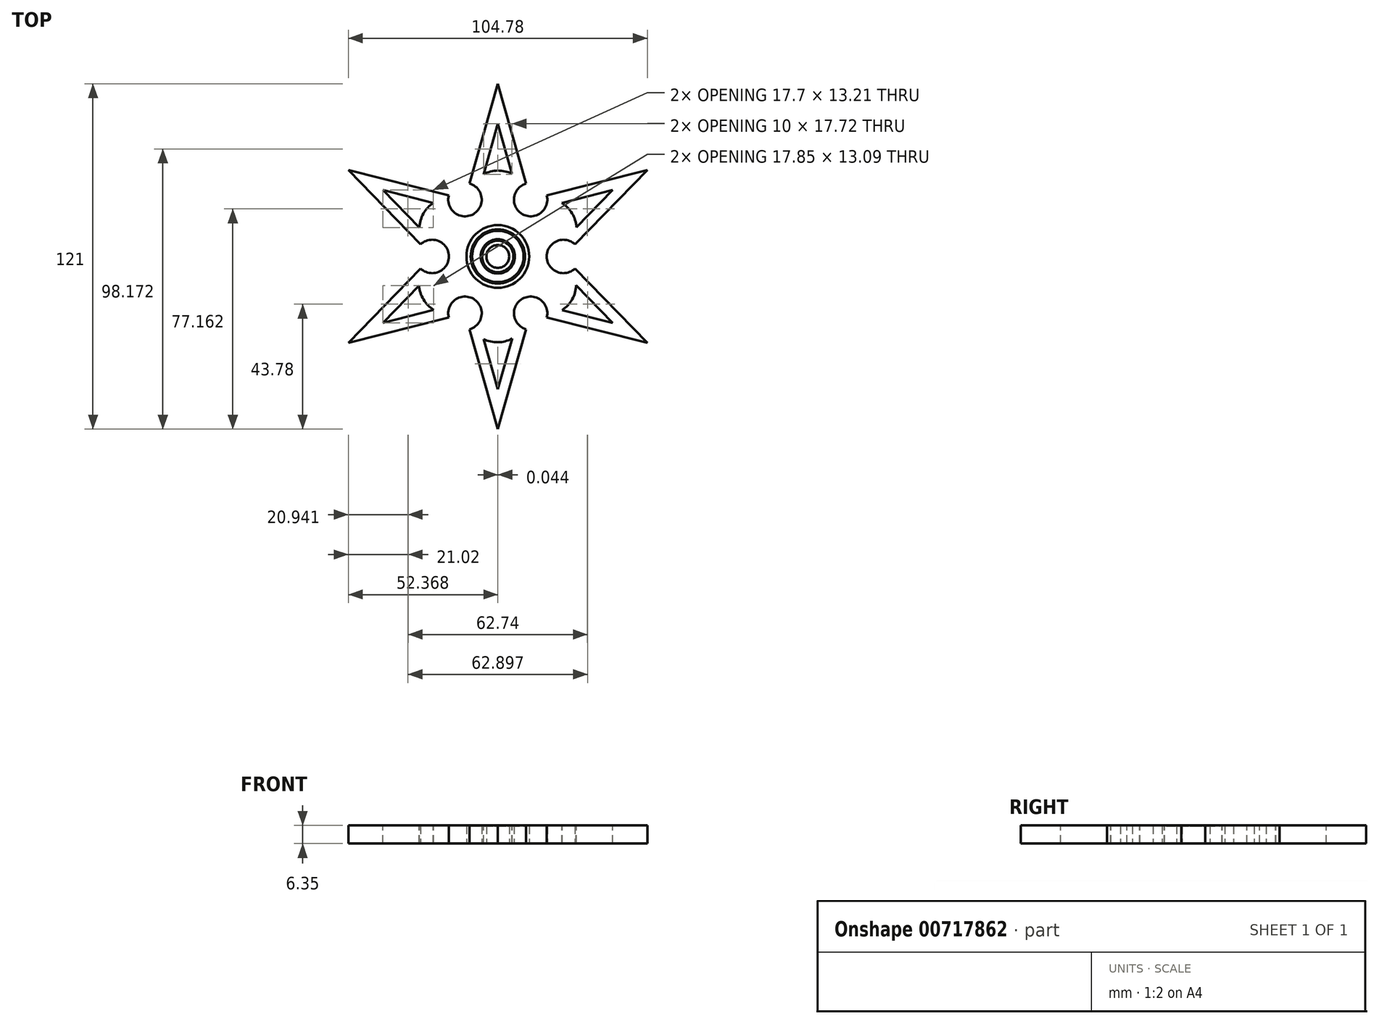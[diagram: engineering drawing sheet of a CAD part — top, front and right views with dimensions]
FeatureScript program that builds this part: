
annotation { "Feature Type Name" : "Feature", "Feature Type Description" : "" }
export const myFeature = defineFeature(function(context is Context, id is Id, definition is map)
    precondition{}
    {
        {
            assignVariable(context, id + "F0", {"name" : "th", "anyValue" : 6.35 * mm});
        }
        {
            var Q0;
            Q0=qCreatedBy(makeId("Top.planeOp"),FACE);
            var sketch = newSketch(context, id + "F1", { "sketchPlane" : qUnion([Q0])});
            skCircle(sketch, "E0", {"center": v(0, 0) * mm, "radius": 4 * mm});
            skCircle(sketch, "E1", {"center": v(0, 0) * mm, "radius": 11 * mm});
            skSolve(sketch);
        }
        {
            var Q0;
            Q0=makeQuery(id+"F1.imprint","IMPRINT",FACE,{"disambiguationData":[TD([[makeQuery(id+"F1.imprint","IMPRINT",EDGE,{"derivedFrom":sQuery(id+"F1.wireOp",EDGE,"E0")}),-1.0]])]});
            extrude(context, id + "F2", {"entities" : qUnion([Q0]), "depth" : getVariable(context, 'th'), "offsetDistance" : 25.4 * mm});
        }
        {
            var Q0;
            Q0=qCreatedBy(makeId("Right.planeOp"),FACE);
            var sketch = newSketch(context, id + "F3", { "sketchPlane" : qUnion([Q0])});
            skLineSegment(sketch, "E2", {"start": v(0, 0) * mm, "end": v(0, 6.35) * mm});
            skLineSegment(sketch, "E3", {"start": v(0, 6.35) * mm, "end": v(4, 6.35) * mm});
            skLineSegment(sketch, "E4", {"start": v(4, 6.35) * mm, "end": v(5.75, 6.35) * mm});
            skLineSegment(sketch, "E5", {"start": v(5.75, 6.35) * mm, "end": v(9.25, 6.35) * mm});
            skLineSegment(sketch, "E6", {"start": v(9.25, 6.35) * mm, "end": v(11, 6.35) * mm});
            skCircle(sketch, "E7", {"center": v(5.75, 6.35) * mm, "radius": 0.25 * mm});
            skCircle(sketch, "E8", {"center": v(9.25, 6.35) * mm, "radius": 0.25 * mm});
            skSolve(sketch);
        }
        {
            var Q0;
            Q0 = qSketchRegion(id + "F3", true);
            var Q1;
            Q1=sQuery(id+"F3.wireOp",EDGE,"E2");
            revolve(context, id + "F4", {"operationType" : NewBodyOperationType.REMOVE, "surfaceOperationType" : NewSurfaceOperationType.NEW, "entities" : qUnion([Q0]), "axis" : qUnion([Q1]), "revolveType" : RevolveType.FULL, "oppositeDirection" : true});
        }
        {
            var Q0;
            Q0=qCreatedBy(makeId("Top.planeOp"),FACE);
            var sketch = newSketch(context, id + "F5", { "sketchPlane" : qUnion([Q0])});
            skCircle(sketch, "E9", {"center": v(0, 0) * mm, "radius": 16.5 * mm});
            skLineSegment(sketch, "E10", {"start": v(0, 16.5) * mm, "end": v(0, 60.5) * mm});
            skLineSegment(sketch, "E11", {"start": v(0, 60.5) * mm, "end": v(9.9, 25.56) * mm});
            skLineSegment(sketch, "E12", {"start": v(0, 60.5) * mm, "end": v(-9.9, 25.56) * mm});
            skLineSegment(sketch, "E13.1.0", {"start": v(-52.4, 30.25) * mm, "end": v(-17.18, 21.36) * mm});
            skLineSegment(sketch, "E13.1.1", {"start": v(-52.4, 30.25) * mm, "end": v(-27.08, 4.2) * mm});
            skLineSegment(sketch, "E13.2.0", {"start": v(-52.4, -30.25) * mm, "end": v(-27.08, -4.2) * mm});
            skLineSegment(sketch, "E13.2.1", {"start": v(-52.4, -30.25) * mm, "end": v(-17.18, -21.36) * mm});
            skLineSegment(sketch, "E14.2.3.0", {"start": v(0, -60.5) * mm, "end": v(-9.9, -25.56) * mm});
            skLineSegment(sketch, "E14.3.3.0", {"start": v(0, -60.5) * mm, "end": v(9.9, -25.56) * mm});
            skLineSegment(sketch, "E14.2.4.0", {"start": v(52.4, -30.25) * mm, "end": v(17.18, -21.36) * mm});
            skLineSegment(sketch, "E14.3.4.0", {"start": v(52.4, -30.25) * mm, "end": v(27.08, -4.2) * mm});
            skLineSegment(sketch, "E14.2.5.0", {"start": v(52.4, 30.25) * mm, "end": v(27.08, 4.2) * mm});
            skLineSegment(sketch, "E14.3.5.0", {"start": v(52.4, 30.25) * mm, "end": v(17.18, 21.36) * mm});
            skArc(sketch, "E15", {"start": v(17.18, -21.36) * mm, "mid": v(8.58, -14.85) * mm, "end": v(9.9, -25.56) * mm});
            skArc(sketch, "E16.1.0", {"start": v(27.08, 4.2) * mm, "mid": v(17.15, 0) * mm, "end": v(27.08, -4.2) * mm});
            skArc(sketch, "E16.2.0", {"start": v(9.9, 25.56) * mm, "mid": v(8.58, 14.85) * mm, "end": v(17.18, 21.36) * mm});
            skArc(sketch, "E17.1.3.0", {"start": v(-17.18, 21.36) * mm, "mid": v(-8.58, 14.85) * mm, "end": v(-9.9, 25.56) * mm});
            skArc(sketch, "E17.1.4.0", {"start": v(-27.08, -4.2) * mm, "mid": v(-17.15, 0) * mm, "end": v(-27.08, 4.2) * mm});
            skArc(sketch, "E17.1.5.0", {"start": v(-9.9, -25.56) * mm, "mid": v(-8.58, -14.85) * mm, "end": v(-17.18, -21.36) * mm});
            skLineSegment(sketch, "E18.trimOffspring", {"start": v(-5.83, -18.49) * mm, "end": v(8.58, -14.85) * mm});
            skLineSegment(sketch, "E19.trimOffspring", {"start": v(-13.1, -14.29) * mm, "end": v(-17.15, 0) * mm});
            skLineSegment(sketch, "E20.trimOffspring", {"start": v(-18.93, 4.2) * mm, "end": v(-8.58, 14.85) * mm});
            skLineSegment(sketch, "E21.trimOffspring", {"start": v(-18.93, -4.2) * mm, "end": v(-8.58, -14.85) * mm});
            skLineSegment(sketch, "E22.trimOffspring", {"start": v(-13.1, 14.29) * mm, "end": v(-17.15, 0) * mm});
            skLineSegment(sketch, "E23.trimOffspring", {"start": v(-5.83, 18.49) * mm, "end": v(8.58, 14.85) * mm});
            skLineSegment(sketch, "E24.trimOffspring", {"start": v(13.1, -14.29) * mm, "end": v(17.15, 0) * mm});
            skLineSegment(sketch, "E25.trimOffspring", {"start": v(5.83, -18.49) * mm, "end": v(-8.58, -14.85) * mm});
            skLineSegment(sketch, "E26.trimOffspring", {"start": v(5.83, 18.49) * mm, "end": v(-8.58, 14.85) * mm});
            skLineSegment(sketch, "E27.trimOffspring", {"start": v(13.1, 14.29) * mm, "end": v(17.15, 0) * mm});
            skLineSegment(sketch, "E28.trimOffspring", {"start": v(18.93, 4.2) * mm, "end": v(8.58, 14.85) * mm});
            skLineSegment(sketch, "E29.trimOffspring", {"start": v(18.93, -4.2) * mm, "end": v(8.58, -14.85) * mm});
            skCircle(sketch, "E30", {"center": v(0, 0) * mm, "radius": 11 * mm});
            skSolve(sketch);
        }
        {
            var Q0;
            {var subQ0=sQuery(id+"F5.wireOp",EDGE,"E11");Q0=makeQuery(id+"F5.imprint","IMPRINT",FACE,{"disambiguationData":[TD([[makeQuery(id+"F5.imprint","IMPRINT",EDGE,{"derivedFrom":subQ0}),-1.0]])]});}
            var Q1;
            {var subQ0=sQuery(id+"F5.wireOp",EDGE,"E12");Q1=makeQuery(id+"F5.imprint","IMPRINT",FACE,{"disambiguationData":[TD([[makeQuery(id+"F5.imprint","IMPRINT",EDGE,{"derivedFrom":subQ0}),1.0]])]});}
            var Q2;
            {var subQ7=sQuery(id+"F5.wireOp",EDGE,"E13.1.0");Q2=makeQuery(id+"F5.imprint","IMPRINT",FACE,{"disambiguationData":[TD([[makeQuery(id+"F5.imprint","IMPRINT",EDGE,{"derivedFrom":subQ7}),-1.0]])]});}
            var Q3;
            {var subQ4=sQuery(id+"F5.wireOp",EDGE,"E13.2.0");Q3=makeQuery(id+"F5.imprint","IMPRINT",FACE,{"disambiguationData":[TD([[makeQuery(id+"F5.imprint","IMPRINT",EDGE,{"derivedFrom":subQ4}),-1.0]])]});}
            var Q4;
            {var subQ1=sQuery(id+"F5.wireOp",EDGE,"E14.2.3.0");Q4=makeQuery(id+"F5.imprint","IMPRINT",FACE,{"disambiguationData":[TD([[makeQuery(id+"F5.imprint","IMPRINT",EDGE,{"derivedFrom":subQ1}),-1.0]])]});}
            var Q5;
            {var subQ5=sQuery(id+"F5.wireOp",EDGE,"E14.2.4.0");Q5=makeQuery(id+"F5.imprint","IMPRINT",FACE,{"disambiguationData":[TD([[makeQuery(id+"F5.imprint","IMPRINT",EDGE,{"derivedFrom":subQ5}),-1.0]])]});}
            var Q6;
            {var subQ1=sQuery(id+"F5.wireOp",EDGE,"E14.2.5.0");Q6=makeQuery(id+"F5.imprint","IMPRINT",FACE,{"disambiguationData":[TD([[makeQuery(id+"F5.imprint","IMPRINT",EDGE,{"derivedFrom":subQ1}),-1.0]])]});}
            var Q7;
            {var subQ0=sQuery(id+"F5.wireOp",EDGE,"E24.trimOffspring");var subQ1=sQuery(id+"F5.wireOp",EDGE,"E9");var subQ2=makeQuery(id+"F5.imprint","INTERSECT",VERTEX,{"derivedFrom":[subQ1,subQ0]});Q7=makeQuery(id+"F5.imprint","IMPRINT",FACE,{"disambiguationData":[TD([[makeQuery(id+"F5.imprint","IMPRINT",EDGE,{"disambiguationData":[TD([[subQ2,-1.0]])],"derivedFrom":subQ1}),-1.0]])]});}
            var Q8;
            {var subQ0=sQuery(id+"F5.wireOp",EDGE,"E28.trimOffspring");var subQ1=sQuery(id+"F5.wireOp",EDGE,"E9");var subQ2=makeQuery(id+"F5.imprint","INTERSECT",VERTEX,{"derivedFrom":[subQ1,subQ0]});Q8=makeQuery(id+"F5.imprint","IMPRINT",FACE,{"disambiguationData":[TD([[makeQuery(id+"F5.imprint","IMPRINT",EDGE,{"disambiguationData":[TD([[subQ2,-1.0]])],"derivedFrom":subQ1}),-1.0]])]});}
            var Q9;
            {var subQ0=sQuery(id+"F5.wireOp",EDGE,"E26.trimOffspring");var subQ1=sQuery(id+"F5.wireOp",EDGE,"E9");var subQ2=makeQuery(id+"F5.imprint","INTERSECT",VERTEX,{"derivedFrom":[subQ1,subQ0]});Q9=makeQuery(id+"F5.imprint","IMPRINT",FACE,{"disambiguationData":[TD([[makeQuery(id+"F5.imprint","IMPRINT",EDGE,{"disambiguationData":[TD([[subQ2,-1.0]])],"derivedFrom":subQ1}),-1.0]])]});}
            var Q10;
            {var subQ0=sQuery(id+"F5.wireOp",EDGE,"E22.trimOffspring");var subQ1=sQuery(id+"F5.wireOp",EDGE,"E9");var subQ2=makeQuery(id+"F5.imprint","INTERSECT",VERTEX,{"derivedFrom":[subQ1,subQ0]});Q10=makeQuery(id+"F5.imprint","IMPRINT",FACE,{"disambiguationData":[TD([[makeQuery(id+"F5.imprint","IMPRINT",EDGE,{"disambiguationData":[TD([[subQ2,-1.0]])],"derivedFrom":subQ1}),-1.0]])]});}
            var Q11;
            {var subQ0=sQuery(id+"F5.wireOp",EDGE,"E21.trimOffspring");var subQ1=sQuery(id+"F5.wireOp",EDGE,"E9");var subQ2=makeQuery(id+"F5.imprint","INTERSECT",VERTEX,{"derivedFrom":[subQ1,subQ0]});Q11=makeQuery(id+"F5.imprint","IMPRINT",FACE,{"disambiguationData":[TD([[makeQuery(id+"F5.imprint","IMPRINT",EDGE,{"disambiguationData":[TD([[subQ2,-1.0]])],"derivedFrom":subQ1}),-1.0]])]});}
            var Q12;
            {var subQ0=sQuery(id+"F5.wireOp",EDGE,"E29.trimOffspring");var subQ1=sQuery(id+"F5.wireOp",EDGE,"E9");var subQ2=makeQuery(id+"F5.imprint","INTERSECT",VERTEX,{"derivedFrom":[subQ1,subQ0]});Q12=makeQuery(id+"F5.imprint","IMPRINT",FACE,{"disambiguationData":[TD([[makeQuery(id+"F5.imprint","IMPRINT",EDGE,{"disambiguationData":[TD([[subQ2,1.0]])],"derivedFrom":subQ1}),-1.0]])]});}
            var Q13;
            {var subQ1=sQuery(id+"F5.wireOp",EDGE,"E15");var subQ3=sQuery(id+"F5.wireOp",EDGE,"E24.trimOffspring");var subQ4=makeQuery(id+"F5.imprint","INTERSECT",VERTEX,{"derivedFrom":[subQ1,subQ3]});Q13=makeQuery(id+"F5.imprint","IMPRINT",FACE,{"disambiguationData":[TD([[makeQuery(id+"F5.imprint","IMPRINT",EDGE,{"disambiguationData":[TD([[subQ4,-1.0]])],"derivedFrom":subQ3}),1.0]])]});}
            var Q14;
            {var subQ0=sQuery(id+"F5.wireOp",EDGE,"E18.trimOffspring");var subQ5=makeQuery(id+"F5.imprint","INTERSECT",VERTEX,{"derivedFrom":[sQuery(id+"F5.wireOp",EDGE,"E9"),subQ0]});Q14=makeQuery(id+"F5.imprint","IMPRINT",FACE,{"disambiguationData":[TD([[makeQuery(id+"F5.imprint","IMPRINT",EDGE,{"disambiguationData":[TD([[subQ5,1.0]])],"derivedFrom":subQ0}),-1.0]])]});}
            var Q15;
            {var subQ0=sQuery(id+"F5.wireOp",EDGE,"E27.trimOffspring");var subQ5=makeQuery(id+"F5.imprint","INTERSECT",VERTEX,{"derivedFrom":[sQuery(id+"F5.wireOp",EDGE,"E9"),subQ0]});Q15=makeQuery(id+"F5.imprint","IMPRINT",FACE,{"disambiguationData":[TD([[makeQuery(id+"F5.imprint","IMPRINT",EDGE,{"disambiguationData":[TD([[subQ5,1.0]])],"derivedFrom":subQ0}),1.0]])]});}
            var Q16;
            {var subQ0=sQuery(id+"F5.wireOp",EDGE,"E24.trimOffspring");var subQ5=makeQuery(id+"F5.imprint","INTERSECT",VERTEX,{"derivedFrom":[sQuery(id+"F5.wireOp",EDGE,"E9"),subQ0]});Q16=makeQuery(id+"F5.imprint","IMPRINT",FACE,{"disambiguationData":[TD([[makeQuery(id+"F5.imprint","IMPRINT",EDGE,{"disambiguationData":[TD([[subQ5,1.0]])],"derivedFrom":subQ0}),-1.0]])]});}
            var Q17;
            {var subQ1=sQuery(id+"F5.wireOp",EDGE,"E16.2.0");var subQ3=sQuery(id+"F5.wireOp",EDGE,"E27.trimOffspring");var subQ4=makeQuery(id+"F5.imprint","INTERSECT",VERTEX,{"derivedFrom":[subQ1,subQ3]});Q17=makeQuery(id+"F5.imprint","IMPRINT",FACE,{"disambiguationData":[TD([[makeQuery(id+"F5.imprint","IMPRINT",EDGE,{"disambiguationData":[TD([[subQ4,-1.0]])],"derivedFrom":subQ3}),-1.0]])]});}
            var Q18;
            {var subQ0=sQuery(id+"F5.wireOp",EDGE,"E20.trimOffspring");var subQ5=makeQuery(id+"F5.imprint","INTERSECT",VERTEX,{"derivedFrom":[sQuery(id+"F5.wireOp",EDGE,"E9"),subQ0]});Q18=makeQuery(id+"F5.imprint","IMPRINT",FACE,{"disambiguationData":[TD([[makeQuery(id+"F5.imprint","IMPRINT",EDGE,{"disambiguationData":[TD([[subQ5,1.0]])],"derivedFrom":subQ0}),1.0]])]});}
            var Q19;
            {var subQ1=sQuery(id+"F5.wireOp",EDGE,"E17.1.3.0");var subQ3=sQuery(id+"F5.wireOp",EDGE,"E23.trimOffspring");var subQ4=makeQuery(id+"F5.imprint","INTERSECT",VERTEX,{"derivedFrom":[subQ1,subQ3]});Q19=makeQuery(id+"F5.imprint","IMPRINT",FACE,{"disambiguationData":[TD([[makeQuery(id+"F5.imprint","IMPRINT",EDGE,{"disambiguationData":[TD([[subQ4,1.0]])],"derivedFrom":subQ1}),-1.0]])]});}
            var Q20;
            {var subQ0=sQuery(id+"F5.wireOp",EDGE,"E19.trimOffspring");var subQ5=makeQuery(id+"F5.imprint","INTERSECT",VERTEX,{"derivedFrom":[sQuery(id+"F5.wireOp",EDGE,"E9"),subQ0]});Q20=makeQuery(id+"F5.imprint","IMPRINT",FACE,{"disambiguationData":[TD([[makeQuery(id+"F5.imprint","IMPRINT",EDGE,{"disambiguationData":[TD([[subQ5,1.0]])],"derivedFrom":subQ0}),1.0]])]});}
            var Q21;
            {var subQ1=sQuery(id+"F5.wireOp",EDGE,"E17.1.4.0");var subQ3=sQuery(id+"F5.wireOp",EDGE,"E20.trimOffspring");var subQ4=makeQuery(id+"F5.imprint","INTERSECT",VERTEX,{"derivedFrom":[subQ1,subQ3]});Q21=makeQuery(id+"F5.imprint","IMPRINT",FACE,{"disambiguationData":[TD([[makeQuery(id+"F5.imprint","IMPRINT",EDGE,{"disambiguationData":[TD([[subQ4,-1.0]])],"derivedFrom":subQ3}),-1.0]])]});}
            var Q22;
            {var subQ0=sQuery(id+"F5.wireOp",EDGE,"E18.trimOffspring");var subQ1=sQuery(id+"F5.wireOp",EDGE,"E17.1.5.0");var subQ2=makeQuery(id+"F5.imprint","INTERSECT",VERTEX,{"derivedFrom":[subQ1,subQ0]});Q22=makeQuery(id+"F5.imprint","IMPRINT",FACE,{"disambiguationData":[TD([[makeQuery(id+"F5.imprint","IMPRINT",EDGE,{"disambiguationData":[TD([[subQ2,-1.0]])],"derivedFrom":subQ0}),1.0]])]});}
            var Q23;
            {var subQ0=sQuery(id+"F5.wireOp",EDGE,"E19.trimOffspring");var subQ1=sQuery(id+"F5.wireOp",EDGE,"E17.1.5.0");var subQ2=makeQuery(id+"F5.imprint","INTERSECT",VERTEX,{"derivedFrom":[subQ1,subQ0]});Q23=makeQuery(id+"F5.imprint","IMPRINT",FACE,{"disambiguationData":[TD([[makeQuery(id+"F5.imprint","IMPRINT",EDGE,{"disambiguationData":[TD([[subQ2,-1.0]])],"derivedFrom":subQ0}),-1.0]])]});}
            var Q24;
            {var subQ0=sQuery(id+"F5.wireOp",EDGE,"E9");var subQ8=makeQuery(id+"F5.imprint","INTERSECT",VERTEX,{"derivedFrom":[subQ0,sQuery(id+"F5.wireOp",EDGE,"E24.trimOffspring")]});Q24=makeQuery(id+"F5.imprint","IMPRINT",FACE,{"disambiguationData":[TD([[makeQuery(id+"F5.imprint","IMPRINT",EDGE,{"disambiguationData":[TD([[subQ8,1.0]])],"derivedFrom":subQ0}),1.0]])]});}
            var Q25;
            {var subQ0=sQuery(id+"F5.wireOp",EDGE,"E20.trimOffspring");var subQ1=sQuery(id+"F5.wireOp",EDGE,"E9");var subQ2=makeQuery(id+"F5.imprint","INTERSECT",VERTEX,{"derivedFrom":[subQ1,subQ0]});Q25=makeQuery(id+"F5.imprint","IMPRINT",FACE,{"disambiguationData":[TD([[makeQuery(id+"F5.imprint","IMPRINT",EDGE,{"disambiguationData":[TD([[subQ2,-1.0]])],"derivedFrom":subQ1}),-1.0]])]});}
            var Q26;
            {var subQ0=sQuery(id+"F5.wireOp",EDGE,"E9");var subQ1=sQuery(id+"F5.wireOp",EDGE,"E10");var subQ2=makeQuery(id+"F5.imprint","INTERSECT",VERTEX,{"derivedFrom":[subQ1,subQ0]});Q26=makeQuery(id+"F5.imprint","IMPRINT",FACE,{"disambiguationData":[TD([[makeQuery(id+"F5.imprint","IMPRINT",EDGE,{"disambiguationData":[TD([[subQ2,-1.0]])],"derivedFrom":subQ0}),-1.0]])]});}
            var Q27;
            {var subQ0=sQuery(id+"F5.wireOp",EDGE,"E9");var subQ1=sQuery(id+"F5.wireOp",EDGE,"E10");var subQ2=makeQuery(id+"F5.imprint","INTERSECT",VERTEX,{"derivedFrom":[subQ1,subQ0]});Q27=makeQuery(id+"F5.imprint","IMPRINT",FACE,{"disambiguationData":[TD([[makeQuery(id+"F5.imprint","IMPRINT",EDGE,{"disambiguationData":[TD([[subQ2,1.0]])],"derivedFrom":subQ0}),-1.0]])]});}
            var Q28;
            {var subQ1=sQuery(id+"F5.wireOp",EDGE,"E16.2.0");var subQ3=sQuery(id+"F5.wireOp",EDGE,"E26.trimOffspring");var subQ4=makeQuery(id+"F5.imprint","INTERSECT",VERTEX,{"derivedFrom":[subQ1,subQ3]});Q28=makeQuery(id+"F5.imprint","IMPRINT",FACE,{"disambiguationData":[TD([[makeQuery(id+"F5.imprint","IMPRINT",EDGE,{"disambiguationData":[TD([[subQ4,-1.0]])],"derivedFrom":subQ1}),-1.0]])]});}
            var Q29;
            {var subQ0=sQuery(id+"F5.wireOp",EDGE,"E19.trimOffspring");var subQ1=sQuery(id+"F5.wireOp",EDGE,"E9");var subQ2=makeQuery(id+"F5.imprint","INTERSECT",VERTEX,{"derivedFrom":[subQ1,subQ0]});Q29=makeQuery(id+"F5.imprint","IMPRINT",FACE,{"disambiguationData":[TD([[makeQuery(id+"F5.imprint","IMPRINT",EDGE,{"disambiguationData":[TD([[subQ2,-1.0]])],"derivedFrom":subQ1}),-1.0]])]});}
            var Q30;
            {var subQ0=sQuery(id+"F5.wireOp",EDGE,"E25.trimOffspring");var subQ1=sQuery(id+"F5.wireOp",EDGE,"E9");var subQ2=makeQuery(id+"F5.imprint","INTERSECT",VERTEX,{"derivedFrom":[subQ1,subQ0]});Q30=makeQuery(id+"F5.imprint","IMPRINT",FACE,{"disambiguationData":[TD([[makeQuery(id+"F5.imprint","IMPRINT",EDGE,{"disambiguationData":[TD([[subQ2,-1.0]])],"derivedFrom":subQ1}),-1.0]])]});}
            var Q31;
            {var subQ0=sQuery(id+"F5.wireOp",EDGE,"E24.trimOffspring");var subQ1=sQuery(id+"F5.wireOp",EDGE,"E9");var subQ2=makeQuery(id+"F5.imprint","INTERSECT",VERTEX,{"derivedFrom":[subQ1,subQ0]});Q31=makeQuery(id+"F5.imprint","IMPRINT",FACE,{"disambiguationData":[TD([[makeQuery(id+"F5.imprint","IMPRINT",EDGE,{"disambiguationData":[TD([[subQ2,1.0]])],"derivedFrom":subQ1}),-1.0]])]});}
            var Q32;
            {var subQ0=sQuery(id+"F5.wireOp",EDGE,"E27.trimOffspring");var subQ1=sQuery(id+"F5.wireOp",EDGE,"E9");var subQ2=makeQuery(id+"F5.imprint","INTERSECT",VERTEX,{"derivedFrom":[subQ1,subQ0]});Q32=makeQuery(id+"F5.imprint","IMPRINT",FACE,{"disambiguationData":[TD([[makeQuery(id+"F5.imprint","IMPRINT",EDGE,{"disambiguationData":[TD([[subQ2,-1.0]])],"derivedFrom":subQ1}),-1.0]])]});}
            extrude(context, id + "F6", {"entities" : qUnion([Q0, Q1, Q2, Q3, Q4, Q5, Q6, Q7, Q8, Q9, Q10, Q11, Q12, Q13, Q14, Q15, Q16, Q17, Q18, Q19, Q20, Q21, Q22, Q23, Q24, Q25, Q26, Q27, Q28, Q29, Q30, Q31, Q32]), "depth" : getVariable(context, 'th'), "offsetDistance" : 25.4 * mm});
        }
        {
            var Q0;
            Q0=makeQuery(id+"F6.opExtrude","CAP_FACE",FACE,{"disambiguationData":[OSD([sQuery(id+"F5.wireOp",EDGE,"E11"),sQuery(id+"F5.wireOp",EDGE,"E12"),sQuery(id+"F5.wireOp",EDGE,"E13.1.0"),sQuery(id+"F5.wireOp",EDGE,"E13.1.1"),sQuery(id+"F5.wireOp",EDGE,"E13.2.0"),sQuery(id+"F5.wireOp",EDGE,"E13.2.1"),sQuery(id+"F5.wireOp",EDGE,"E14.2.3.0"),sQuery(id+"F5.wireOp",EDGE,"E14.3.3.0"),sQuery(id+"F5.wireOp",EDGE,"E14.2.4.0"),sQuery(id+"F5.wireOp",EDGE,"E14.3.4.0"),sQuery(id+"F5.wireOp",EDGE,"E14.2.5.0"),sQuery(id+"F5.wireOp",EDGE,"E14.3.5.0"),sQuery(id+"F5.wireOp",EDGE,"E15"),sQuery(id+"F5.wireOp",EDGE,"E16.1.0"),sQuery(id+"F5.wireOp",EDGE,"E16.2.0"),sQuery(id+"F5.wireOp",EDGE,"E17.1.3.0"),sQuery(id+"F5.wireOp",EDGE,"E17.1.4.0"),sQuery(id+"F5.wireOp",EDGE,"E17.1.5.0")])],"isStart":false});
            var sketch = newSketch(context, id + "F7", { "sketchPlane" : qUnion([Q0])});
            skPoint(sketch, "E31.center", {"position": v(0, 0) * mm});
            skLineSegment(sketch, "E32.0", {"start": v(-27.58, -10.18) * mm, "end": v(-40.3, -23.26) * mm});
            skLineSegment(sketch, "E32.2", {"start": v(-22.44, -18.76) * mm, "end": v(-40.3, -23.26) * mm});
            skArc(sketch, "E33", {"start": v(-27.58, -10.18) * mm, "mid": v(-26.04, -15.08) * mm, "end": v(-22.44, -18.76) * mm});
            skLineSegment(sketch, "E34.1.0", {"start": v(-4.98, -28.97) * mm, "end": v(0, -46.53) * mm});
            skLineSegment(sketch, "E34.1.1", {"start": v(5.02, -28.81) * mm, "end": v(0, -46.53) * mm});
            skArc(sketch, "E34.1.2", {"start": v(-4.98, -28.97) * mm, "mid": v(0.04, -30.1) * mm, "end": v(5.02, -28.81) * mm});
            skLineSegment(sketch, "E34.2.0", {"start": v(22.6, -18.8) * mm, "end": v(40.3, -23.27) * mm});
            skLineSegment(sketch, "E34.2.1", {"start": v(27.47, -10.06) * mm, "end": v(40.3, -23.27) * mm});
            skArc(sketch, "E34.2.2", {"start": v(22.6, -18.8) * mm, "mid": v(26.08, -15.01) * mm, "end": v(27.47, -10.06) * mm});
            skLineSegment(sketch, "E34.3.0", {"start": v(27.58, 10.18) * mm, "end": v(40.3, 23.26) * mm});
            skLineSegment(sketch, "E34.3.1", {"start": v(22.44, 18.76) * mm, "end": v(40.3, 23.26) * mm});
            skArc(sketch, "E34.3.2", {"start": v(27.58, 10.18) * mm, "mid": v(26.04, 15.08) * mm, "end": v(22.44, 18.76) * mm});
            skLineSegment(sketch, "E34.4.0", {"start": v(4.98, 28.97) * mm, "end": v(0, 46.53) * mm});
            skLineSegment(sketch, "E34.4.1", {"start": v(-5.02, 28.81) * mm, "end": v(0, 46.53) * mm});
            skArc(sketch, "E34.4.2", {"start": v(4.98, 28.97) * mm, "mid": v(-0.04, 30.1) * mm, "end": v(-5.02, 28.81) * mm});
            skLineSegment(sketch, "E34.5.0", {"start": v(-22.6, 18.8) * mm, "end": v(-40.3, 23.27) * mm});
            skLineSegment(sketch, "E34.5.1", {"start": v(-27.47, 10.06) * mm, "end": v(-40.3, 23.27) * mm});
            skArc(sketch, "E34.5.2", {"start": v(-22.6, 18.8) * mm, "mid": v(-26.08, 15.01) * mm, "end": v(-27.47, 10.06) * mm});
            skSolve(sketch);
        }
        {
            var Q0;
            Q0=makeQuery(id+"F7.imprint","IMPRINT",FACE,{"disambiguationData":[TD([[makeQuery(id+"F7.imprint","IMPRINT",EDGE,{"derivedFrom":sQuery(id+"F7.wireOp",EDGE,"E34.2.0")}),1.0]])]});
            var Q1;
            Q1=makeQuery(id+"F7.imprint","IMPRINT",FACE,{"disambiguationData":[TD([[makeQuery(id+"F7.imprint","IMPRINT",EDGE,{"derivedFrom":sQuery(id+"F7.wireOp",EDGE,"E34.1.0")}),1.0]])]});
            var Q2;
            Q2=makeQuery(id+"F7.imprint","IMPRINT",FACE,{"disambiguationData":[TD([[makeQuery(id+"F7.imprint","IMPRINT",EDGE,{"derivedFrom":sQuery(id+"F7.wireOp",EDGE,"E32.0")}),1.0]])]});
            var Q3;
            Q3=makeQuery(id+"F7.imprint","IMPRINT",FACE,{"disambiguationData":[TD([[makeQuery(id+"F7.imprint","IMPRINT",EDGE,{"derivedFrom":sQuery(id+"F7.wireOp",EDGE,"E34.5.0")}),1.0]])]});
            var Q4;
            Q4=makeQuery(id+"F7.imprint","IMPRINT",FACE,{"disambiguationData":[TD([[makeQuery(id+"F7.imprint","IMPRINT",EDGE,{"derivedFrom":sQuery(id+"F7.wireOp",EDGE,"E34.4.0")}),1.0]])]});
            var Q5;
            Q5=makeQuery(id+"F7.imprint","IMPRINT",FACE,{"disambiguationData":[TD([[makeQuery(id+"F7.imprint","IMPRINT",EDGE,{"derivedFrom":sQuery(id+"F7.wireOp",EDGE,"E34.3.0")}),1.0]])]});
            extrude(context, id + "F8", {"entities" : qUnion([Q0, Q1, Q2, Q3, Q4, Q5]), "operationType" : NewBodyOperationType.REMOVE, "oppositeDirection" : true, "depth" : 25.4 * mm, "offsetDistance" : 25.4 * mm});
        }
    });
